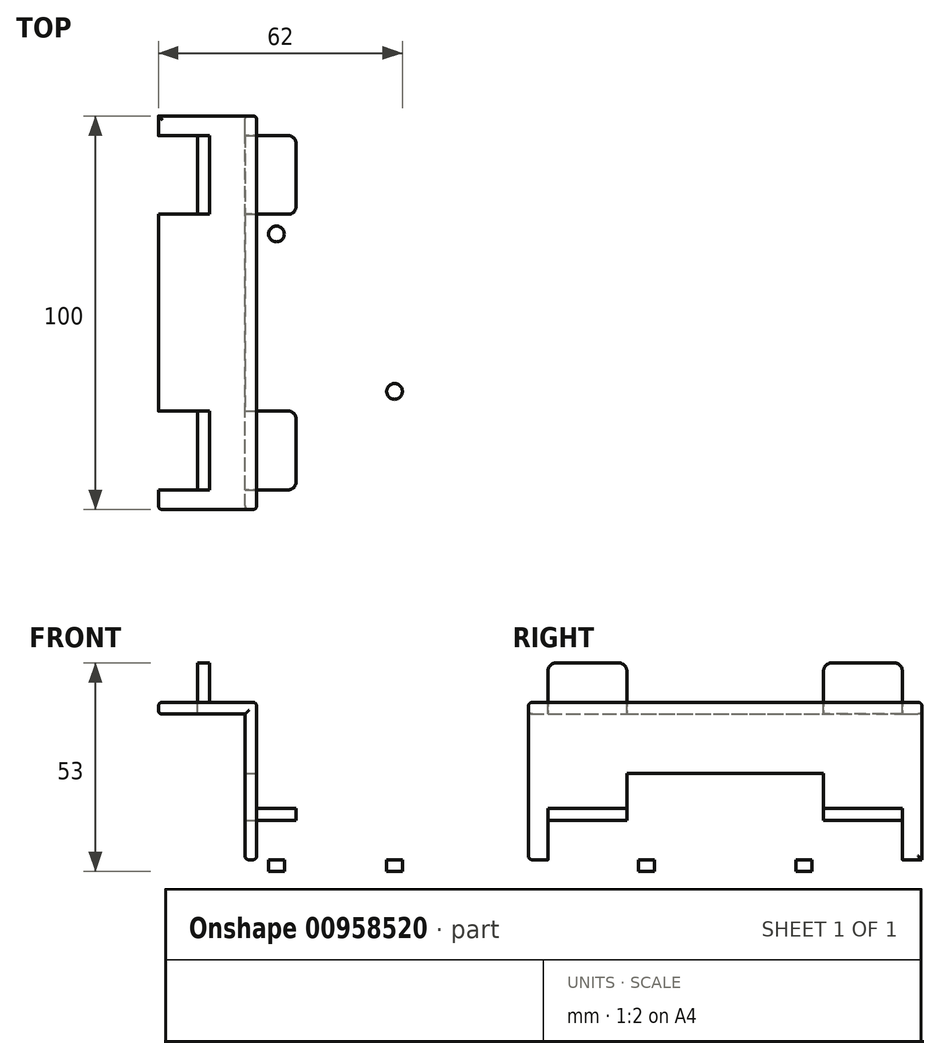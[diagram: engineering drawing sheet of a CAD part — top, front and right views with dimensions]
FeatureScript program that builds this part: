
annotation { "Feature Type Name" : "Feature", "Feature Type Description" : "" }
export const myFeature = defineFeature(function(context is Context, id is Id, definition is map)
    precondition{}
    {
        {
            var Q0;
            Q0=qCreatedBy(makeId("Front.planeOp"),FACE);
            var sketch = newSketch(context, id + "F0", { "sketchPlane" : qUnion([Q0])});
            skLineSegment(sketch, "E0", {"start": v(0, 0) * mm, "end": v(0, 40) * mm});
            skLineSegment(sketch, "E1", {"start": v(0, 40) * mm, "end": v(-25, 40) * mm});
            skLineSegment(sketch, "E2", {"start": v(-25, 40) * mm, "end": v(-25, 37) * mm});
            skLineSegment(sketch, "E3", {"start": v(0, 0) * mm, "end": v(-3, 0) * mm});
            skLineSegment(sketch, "E4", {"start": v(-3, 0) * mm, "end": v(-3, 37) * mm});
            skLineSegment(sketch, "E5", {"start": v(-3, 37) * mm, "end": v(-25, 37) * mm});
            skSolve(sketch);
        }
        {
            var Q0;
            Q0=makeQuery(id+"F0.imprint","IMPRINT",FACE,{"disambiguationData":[TD([[makeQuery(id+"F0.imprint","IMPRINT",EDGE,{"derivedFrom":sQuery(id+"F0.wireOp",EDGE,"E0")}),1.0]])]});
            extrude(context, id + "F1", {"entities" : qUnion([Q0]), "endBound" : BoundingType.SYMMETRIC, "depth" : 100 * mm, "offsetDistance" : 25 * mm});
        }
        {
            var Q0;
            Q0=makeQuery(id+"F1.opExtrude","SWEPT_FACE",FACE,{"disambiguationData":[OSD([sQuery(id+"F0.wireOp",EDGE,"E0")])]});
            var sketch = newSketch(context, id + "F2", { "sketchPlane" : qUnion([Q0])});
            skLineSegment(sketch, "E6.bottom", {"start": v(-45, 0) * mm, "end": v(-25, 0) * mm});
            skLineSegment(sketch, "E6.top", {"start": v(-45, 10) * mm, "end": v(-25, 10) * mm});
            skLineSegment(sketch, "E6.left", {"start": v(-45, 0) * mm, "end": v(-45, 10) * mm});
            skLineSegment(sketch, "E6.right", {"start": v(-25, 0) * mm, "end": v(-25, 10) * mm});
            skLineSegment(sketch, "E7.MirrorCS", {"start": v(25, 0) * mm, "end": v(25, 10) * mm});
            skLineSegment(sketch, "E8.MirrorCS", {"start": v(45, 10) * mm, "end": v(25, 10) * mm});
            skLineSegment(sketch, "E9.MirrorCS", {"start": v(45, 0) * mm, "end": v(45, 10) * mm});
            skLineSegment(sketch, "E10.MirrorCS", {"start": v(45, 0) * mm, "end": v(25, 0) * mm});
            skLineSegment(sketch, "E11.top", {"start": v(-45, 13) * mm, "end": v(-25, 13) * mm});
            skLineSegment(sketch, "E11.left", {"start": v(-45, 10) * mm, "end": v(-45, 13) * mm});
            skLineSegment(sketch, "E11.right", {"start": v(-25, 10) * mm, "end": v(-25, 13) * mm});
            skLineSegment(sketch, "E12.MirrorCS", {"start": v(45, 13) * mm, "end": v(25, 13) * mm});
            skLineSegment(sketch, "E13.MirrorCS", {"start": v(25, 10) * mm, "end": v(25, 13) * mm});
            skLineSegment(sketch, "E14.MirrorCS", {"start": v(45, 10) * mm, "end": v(45, 13) * mm});
            skSolve(sketch);
        }
        {
            var Q0;
            Q0=makeQuery(id+"F2.imprint","IMPRINT",FACE,{"disambiguationData":[TD([[makeQuery(id+"F2.imprint","IMPRINT",EDGE,{"derivedFrom":sQuery(id+"F2.wireOp",EDGE,"E6.bottom")}),1.0]])]});
            var Q1;
            Q1=makeQuery(id+"F2.imprint","IMPRINT",FACE,{"disambiguationData":[TD([[makeQuery(id+"F2.imprint","IMPRINT",EDGE,{"derivedFrom":sQuery(id+"F2.wireOp",EDGE,"E7.MirrorCS")}),-1.0]])]});
            extrude(context, id + "F3", {"entities" : qUnion([Q0, Q1]), "operationType" : NewBodyOperationType.REMOVE, "endBound" : BoundingType.UP_TO_NEXT, "oppositeDirection" : true, "depth" : 25 * mm, "offsetDistance" : 25 * mm});
        }
        {
            var Q0;
            Q0=makeQuery(id+"F2.imprint","IMPRINT",FACE,{"disambiguationData":[TD([[makeQuery(id+"F2.imprint","IMPRINT",EDGE,{"derivedFrom":sQuery(id+"F2.wireOp",EDGE,"E6.top")}),1.0]])]});
            var Q1;
            Q1=makeQuery(id+"F2.imprint","IMPRINT",FACE,{"disambiguationData":[TD([[makeQuery(id+"F2.imprint","IMPRINT",EDGE,{"derivedFrom":sQuery(id+"F2.wireOp",EDGE,"E8.MirrorCS")}),-1.0]])]});
            extrude(context, id + "F4", {"entities" : qUnion([Q0, Q1]), "operationType" : NewBodyOperationType.ADD, "depth" : 10 * mm, "offsetDistance" : 25 * mm});
        }
        {
            var Q0;
            Q0=makeQuery(id+"F1.opExtrude","SWEPT_FACE",FACE,{"disambiguationData":[OSD([sQuery(id+"F0.wireOp",EDGE,"E1")])]});
            var sketch = newSketch(context, id + "F5", { "sketchPlane" : qUnion([Q0])});
            skLineSegment(sketch, "E15.bottom", {"start": v(-25, 45) * mm, "end": v(-15, 45) * mm});
            skLineSegment(sketch, "E15.top", {"start": v(-25, 25) * mm, "end": v(-15, 25) * mm});
            skLineSegment(sketch, "E15.left", {"start": v(-25, 45) * mm, "end": v(-25, 25) * mm});
            skLineSegment(sketch, "E15.right", {"start": v(-15, 45) * mm, "end": v(-15, 25) * mm});
            skLineSegment(sketch, "E16.bottom", {"start": v(-15, 45) * mm, "end": v(-12, 45) * mm});
            skLineSegment(sketch, "E16.top", {"start": v(-15, 25) * mm, "end": v(-12, 25) * mm});
            skLineSegment(sketch, "E16.right", {"start": v(-12, 45) * mm, "end": v(-12, 25) * mm});
            skLineSegment(sketch, "E17.MirrorCS", {"start": v(-25, -25) * mm, "end": v(-15, -25) * mm});
            skLineSegment(sketch, "E18.MirrorCS", {"start": v(-25, -45) * mm, "end": v(-25, -25) * mm});
            skLineSegment(sketch, "E19.MirrorCS", {"start": v(-25, -45) * mm, "end": v(-15, -45) * mm});
            skLineSegment(sketch, "E20.MirrorCS", {"start": v(-15, -45) * mm, "end": v(-15, -25) * mm});
            skLineSegment(sketch, "E21.MirrorCS", {"start": v(-15, -45) * mm, "end": v(-12, -45) * mm});
            skLineSegment(sketch, "E22.MirrorCS", {"start": v(-12, -45) * mm, "end": v(-12, -25) * mm});
            skLineSegment(sketch, "E23.MirrorCS", {"start": v(-15, -25) * mm, "end": v(-12, -25) * mm});
            skSolve(sketch);
        }
        {
            var Q0;
            Q0=makeQuery(id+"F5.imprint","IMPRINT",FACE,{"disambiguationData":[TD([[makeQuery(id+"F5.imprint","IMPRINT",EDGE,{"derivedFrom":sQuery(id+"F5.wireOp",EDGE,"E15.bottom")}),-1.0]])]});
            var Q1;
            Q1=makeQuery(id+"F5.imprint","IMPRINT",FACE,{"disambiguationData":[TD([[makeQuery(id+"F5.imprint","IMPRINT",EDGE,{"derivedFrom":sQuery(id+"F5.wireOp",EDGE,"E17.MirrorCS")}),-1.0]])]});
            extrude(context, id + "F6", {"entities" : qUnion([Q0, Q1]), "operationType" : NewBodyOperationType.REMOVE, "endBound" : BoundingType.UP_TO_NEXT, "oppositeDirection" : true, "depth" : 25 * mm, "offsetDistance" : 25 * mm});
        }
        {
            var Q0;
            Q0=makeQuery(id+"F5.imprint","IMPRINT",FACE,{"disambiguationData":[TD([[makeQuery(id+"F5.imprint","IMPRINT",EDGE,{"derivedFrom":sQuery(id+"F5.wireOp",EDGE,"E16.bottom")}),-1.0]])]});
            var Q1;
            Q1=makeQuery(id+"F5.imprint","IMPRINT",FACE,{"disambiguationData":[TD([[makeQuery(id+"F5.imprint","IMPRINT",EDGE,{"derivedFrom":sQuery(id+"F5.wireOp",EDGE,"E20.MirrorCS")}),-1.0]])]});
            extrude(context, id + "F7", {"entities" : qUnion([Q0, Q1]), "operationType" : NewBodyOperationType.ADD, "depth" : 10 * mm, "offsetDistance" : 25 * mm});
        }
        {
            var Q0;
            Q0=makeQuery(id+"F7.opExtrude","CAP_EDGE",EDGE,{"disambiguationData":[OSD([sQuery(id+"F5.wireOp",EDGE,"E16.top")])],"isStart":false});
            var Q1;
            Q1=makeQuery(id+"F7.opExtrude","CAP_EDGE",EDGE,{"disambiguationData":[OSD([sQuery(id+"F5.wireOp",EDGE,"E16.bottom")])],"isStart":false});
            var Q2;
            Q2=makeQuery(id+"F7.opExtrude","CAP_EDGE",EDGE,{"disambiguationData":[OSD([sQuery(id+"F5.wireOp",EDGE,"E23.MirrorCS")])],"isStart":false});
            var Q3;
            Q3=makeQuery(id+"F7.opExtrude","CAP_EDGE",EDGE,{"disambiguationData":[OSD([sQuery(id+"F5.wireOp",EDGE,"E21.MirrorCS")])],"isStart":false});
            var Q4;
            Q4=makeQuery(id+"F4.opExtrude","CAP_EDGE",EDGE,{"disambiguationData":[OSD([sQuery(id+"F2.wireOp",EDGE,"E11.left")])],"isStart":false});
            var Q5;
            Q5=makeQuery(id+"F4.opExtrude","CAP_EDGE",EDGE,{"disambiguationData":[OSD([sQuery(id+"F2.wireOp",EDGE,"E11.right")])],"isStart":false});
            var Q6;
            Q6=makeQuery(id+"F4.opExtrude","CAP_EDGE",EDGE,{"disambiguationData":[OSD([sQuery(id+"F2.wireOp",EDGE,"E13.MirrorCS")])],"isStart":false});
            var Q7;
            Q7=makeQuery(id+"F4.opExtrude","CAP_EDGE",EDGE,{"disambiguationData":[OSD([sQuery(id+"F2.wireOp",EDGE,"E14.MirrorCS")])],"isStart":false});
            fillet(context, id + "F8", {"entities" : qUnion([Q0, Q1, Q2, Q3, Q4, Q5, Q6, Q7]), "radius" : 2 * mm, "tangentPropagation" : true, "allowEdgeOverflow" : false});
        }
        {
            var Q0;
            Q0=makeQuery(id+"F1.opExtrude","CAP_EDGE",EDGE,{"disambiguationData":[OSD([sQuery(id+"F0.wireOp",EDGE,"E1")])],"isStart":false});
            var Q1;
            Q1=makeQuery(id+"F1.opExtrude","CAP_EDGE",EDGE,{"disambiguationData":[OSD([sQuery(id+"F0.wireOp",EDGE,"E0")])],"isStart":false});
            var Q2;
            Q2=makeQuery(id+"F1.opExtrude","CAP_EDGE",EDGE,{"disambiguationData":[OSD([sQuery(id+"F0.wireOp",EDGE,"E4")])],"isStart":false});
            var Q3;
            Q3=makeQuery(id+"F1.opExtrude","CAP_EDGE",EDGE,{"disambiguationData":[OSD([sQuery(id+"F0.wireOp",EDGE,"E5")])],"isStart":false});
            fillet(context, id + "F9", {"entities" : qUnion([Q0, Q1, Q2, Q3]), "radius" : 1 * mm, "tangentPropagation" : true, "allowEdgeOverflow" : false});
        }
        {
            var Q0;
            {var subQ0=sQuery(id+"F0.wireOp",EDGE,"E5");var subQ1=sQuery(id+"F0.wireOp",EDGE,"E2");Q0=makeQuery(id+"F6.boolean.opBoolean","SPLIT",EDGE,{"disambiguationData":[TD([makeQuery(id+"F6.opExtrude","SWEPT_FACE",FACE,{"disambiguationData":[OSD([sQuery(id+"F5.wireOp",EDGE,"E19.MirrorCS")])]})])],"derivedFrom":makeQuery(id+"F1.opExtrude","SWEPT_EDGE",EDGE,{"disambiguationData":[OSD([subQ1,subQ0])]})});}
            var Q1;
            {var subQ0=sQuery(id+"F0.wireOp",EDGE,"E2");var subQ1=sQuery(id+"F0.wireOp",EDGE,"E1");Q1=makeQuery(id+"F6.boolean.opBoolean","SPLIT",EDGE,{"disambiguationData":[TD([makeQuery(id+"F6.opExtrude","SWEPT_FACE",FACE,{"disambiguationData":[OSD([sQuery(id+"F5.wireOp",EDGE,"E19.MirrorCS")])]})])],"derivedFrom":makeQuery(id+"F1.opExtrude","SWEPT_EDGE",EDGE,{"disambiguationData":[OSD([subQ1,subQ0])]})});}
            fillet(context, id + "F10", {"entities" : qUnion([Q0, Q1]), "radius" : 1 * mm, "tangentPropagation" : true, "allowEdgeOverflow" : false});
        }
        {
            var Q0;
            {var subQ0=sQuery(id+"F0.wireOp",EDGE,"E1");var subQ1=sQuery(id+"F0.wireOp",EDGE,"E2");Q0=makeQuery(id+"F6.boolean.opBoolean","SPLIT",EDGE,{"disambiguationData":[TD([makeQuery(id+"F6.opExtrude","SWEPT_FACE",FACE,{"disambiguationData":[OSD([sQuery(id+"F5.wireOp",EDGE,"E15.top")])]})])],"derivedFrom":makeQuery(id+"F1.opExtrude","SWEPT_EDGE",EDGE,{"disambiguationData":[OSD([subQ0,subQ1])]})});}
            var Q1;
            {var subQ0=sQuery(id+"F0.wireOp",EDGE,"E2");var subQ1=sQuery(id+"F0.wireOp",EDGE,"E5");Q1=makeQuery(id+"F6.boolean.opBoolean","SPLIT",EDGE,{"disambiguationData":[TD([makeQuery(id+"F6.opExtrude","SWEPT_FACE",FACE,{"disambiguationData":[OSD([sQuery(id+"F5.wireOp",EDGE,"E15.top")])]})])],"derivedFrom":makeQuery(id+"F1.opExtrude","SWEPT_EDGE",EDGE,{"disambiguationData":[OSD([subQ0,subQ1])]})});}
            var Q2;
            {var subQ0=sQuery(id+"F0.wireOp",EDGE,"E2");var subQ1=sQuery(id+"F0.wireOp",EDGE,"E1");Q2=makeQuery(id+"F6.boolean.opBoolean","SPLIT",EDGE,{"disambiguationData":[TD([makeQuery(id+"F6.opExtrude","SWEPT_FACE",FACE,{"disambiguationData":[OSD([sQuery(id+"F5.wireOp",EDGE,"E15.bottom")])]})])],"derivedFrom":makeQuery(id+"F1.opExtrude","SWEPT_EDGE",EDGE,{"disambiguationData":[OSD([subQ1,subQ0])]})});}
            var Q3;
            {var subQ0=sQuery(id+"F0.wireOp",EDGE,"E5");var subQ1=sQuery(id+"F0.wireOp",EDGE,"E2");Q3=makeQuery(id+"F6.boolean.opBoolean","SPLIT",EDGE,{"disambiguationData":[TD([makeQuery(id+"F6.opExtrude","SWEPT_FACE",FACE,{"disambiguationData":[OSD([sQuery(id+"F5.wireOp",EDGE,"E15.bottom")])]})])],"derivedFrom":makeQuery(id+"F1.opExtrude","SWEPT_EDGE",EDGE,{"disambiguationData":[OSD([subQ1,subQ0])]})});}
            var Q4;
            Q4=makeQuery(id+"F1.opExtrude","CAP_EDGE",EDGE,{"disambiguationData":[OSD([sQuery(id+"F0.wireOp",EDGE,"E5")])],"isStart":true});
            var Q5;
            Q5=makeQuery(id+"F1.opExtrude","CAP_EDGE",EDGE,{"disambiguationData":[OSD([sQuery(id+"F0.wireOp",EDGE,"E1")])],"isStart":true});
            var Q6;
            Q6=makeQuery(id+"F1.opExtrude","CAP_EDGE",EDGE,{"disambiguationData":[OSD([sQuery(id+"F0.wireOp",EDGE,"E4")])],"isStart":true});
            var Q7;
            Q7=makeQuery(id+"F1.opExtrude","CAP_EDGE",EDGE,{"disambiguationData":[OSD([sQuery(id+"F0.wireOp",EDGE,"E0")])],"isStart":true});
            var Q8;
            {var subQ0=sQuery(id+"F0.wireOp",EDGE,"E4");var subQ1=sQuery(id+"F0.wireOp",EDGE,"E3");Q8=makeQuery(id+"F3.boolean.opBoolean","SPLIT",EDGE,{"disambiguationData":[TD([makeQuery(id+"F3.opExtrude","SWEPT_FACE",FACE,{"disambiguationData":[OSD([sQuery(id+"F2.wireOp",EDGE,"E9.MirrorCS")])]})])],"derivedFrom":makeQuery(id+"F1.opExtrude","SWEPT_EDGE",EDGE,{"disambiguationData":[OSD([subQ1,subQ0])]})});}
            var Q9;
            {var subQ0=sQuery(id+"F0.wireOp",EDGE,"E0");var subQ1=sQuery(id+"F0.wireOp",EDGE,"E3");Q9=makeQuery(id+"F3.boolean.opBoolean","SPLIT",EDGE,{"disambiguationData":[TD([makeQuery(id+"F3.opExtrude","SWEPT_FACE",FACE,{"disambiguationData":[OSD([sQuery(id+"F2.wireOp",EDGE,"E9.MirrorCS")])]})])],"derivedFrom":makeQuery(id+"F1.opExtrude","SWEPT_EDGE",EDGE,{"disambiguationData":[OSD([subQ0,subQ1])]})});}
            var Q10;
            {var subQ0=sQuery(id+"F0.wireOp",EDGE,"E4");var subQ1=sQuery(id+"F0.wireOp",EDGE,"E3");Q10=makeQuery(id+"F3.boolean.opBoolean","SPLIT",EDGE,{"disambiguationData":[TD([makeQuery(id+"F3.opExtrude","SWEPT_FACE",FACE,{"disambiguationData":[OSD([sQuery(id+"F2.wireOp",EDGE,"E6.left")])]})])],"derivedFrom":makeQuery(id+"F1.opExtrude","SWEPT_EDGE",EDGE,{"disambiguationData":[OSD([subQ1,subQ0])]})});}
            var Q11;
            {var subQ0=sQuery(id+"F0.wireOp",EDGE,"E0");var subQ1=sQuery(id+"F0.wireOp",EDGE,"E3");Q11=makeQuery(id+"F3.boolean.opBoolean","SPLIT",EDGE,{"disambiguationData":[TD([makeQuery(id+"F3.opExtrude","SWEPT_FACE",FACE,{"disambiguationData":[OSD([sQuery(id+"F2.wireOp",EDGE,"E6.left")])]})])],"derivedFrom":makeQuery(id+"F1.opExtrude","SWEPT_EDGE",EDGE,{"disambiguationData":[OSD([subQ0,subQ1])]})});}
            fillet(context, id + "F11", {"entities" : qUnion([Q0, Q1, Q2, Q3, Q4, Q5, Q6, Q7, Q8, Q9, Q10, Q11]), "radius" : 1 * mm, "tangentPropagation" : true, "allowEdgeOverflow" : false});
        }
        {
            var Q0;
            Q0=makeQuery(id+"F1.opExtrude","SWEPT_EDGE",EDGE,{"disambiguationData":[OSD([sQuery(id+"F0.wireOp",EDGE,"E0"),sQuery(id+"F0.wireOp",EDGE,"E1")])]});
            fillet(context, id + "F12", {"entities" : qUnion([Q0]), "radius" : 1 * mm, "tangentPropagation" : true, "allowEdgeOverflow" : false});
        }
        {
            var Q0;
            Q0=qCreatedBy(makeId("Right.planeOp"),FACE);
            var sketch = newSketch(context, id + "F13", { "sketchPlane" : qUnion([Q0])});
            skLineSegment(sketch, "E24.bottom", {"start": v(-25, 0) * mm, "end": v(25, 0) * mm});
            skLineSegment(sketch, "E24.top", {"start": v(-25, -3) * mm, "end": v(25, -3) * mm});
            skLineSegment(sketch, "E24.left", {"start": v(-25, 0) * mm, "end": v(-25, -3) * mm});
            skLineSegment(sketch, "E24.right", {"start": v(25, 0) * mm, "end": v(25, -3) * mm});
            skSolve(sketch);
        }
        {
            var Q0;
            Q0=makeQuery(id+"F13.imprint","IMPRINT",FACE,{"disambiguationData":[TD([[makeQuery(id+"F13.imprint","IMPRINT",EDGE,{"derivedFrom":sQuery(id+"F13.wireOp",EDGE,"E24.bottom")}),-1.0]])]});
            extrude(context, id + "F14", {"entities" : qUnion([Q0]), "operationType" : NewBodyOperationType.ADD, "oppositeDirection" : true, "depth" : 23 * mm, "offsetDistance" : 25 * mm});
        }
        {
            var Q0;
            Q0=makeQuery(id+"F14.boolean.opBoolean","MERGE",FACE,{"derivedFrom":[makeQuery(id+"F1.opExtrude","SWEPT_FACE",FACE,{"disambiguationData":[OSD([sQuery(id+"F0.wireOp",EDGE,"E0")])]}),makeQuery(id+"F14.opExtrude","CAP_FACE",FACE,{"disambiguationData":[OSD([sQuery(id+"F13.wireOp",EDGE,"E24.bottom"),sQuery(id+"F13.wireOp",EDGE,"E24.top"),sQuery(id+"F13.wireOp",EDGE,"E24.left"),sQuery(id+"F13.wireOp",EDGE,"E24.right")])],"isStart":true})]});
            var sketch = newSketch(context, id + "F15", { "sketchPlane" : qUnion([Q0])});
            skLineSegment(sketch, "E25.bottom", {"start": v(-25, -3) * mm, "end": v(25, -3) * mm});
            skLineSegment(sketch, "E25.top", {"start": v(-25, 0) * mm, "end": v(25, 0) * mm});
            skLineSegment(sketch, "E25.left", {"start": v(-25, -3) * mm, "end": v(-25, 0) * mm});
            skLineSegment(sketch, "E25.right", {"start": v(25, -3) * mm, "end": v(25, 0) * mm});
            skSolve(sketch);
        }
        {
            var Q0;
            Q0=makeQuery(id+"F15.imprint","IMPRINT",FACE,{"disambiguationData":[TD([[makeQuery(id+"F15.imprint","IMPRINT",EDGE,{"derivedFrom":sQuery(id+"F15.wireOp",EDGE,"E25.bottom")}),1.0]])]});
            extrude(context, id + "F16", {"entities" : qUnion([Q0]), "operationType" : NewBodyOperationType.ADD, "depth" : 40 * mm, "offsetDistance" : 25 * mm});
        }
        {
            var Q0;
            Q0=makeQuery(id+"F16.boolean.opBoolean","MERGE",FACE,{"derivedFrom":[makeQuery(id+"F14.opExtrude","SWEPT_FACE",FACE,{"disambiguationData":[OSD([sQuery(id+"F13.wireOp",EDGE,"E24.top")])]}),makeQuery(id+"F16.opExtrude","SWEPT_FACE",FACE,{"disambiguationData":[OSD([sQuery(id+"F15.wireOp",EDGE,"E25.bottom")])]})]});
            var sketch = newSketch(context, id + "F17", { "sketchPlane" : qUnion([Q0])});
            skLineSegment(sketch, "E26", {"start": v(0, 0) * mm, "end": v(40, 0) * mm, "construction": true});
            skLineSegment(sketch, "E27", {"start": v(20, 25) * mm, "end": v(20, 0) * mm, "construction": true});
            skPoint(sketch, "E27.startSnap0", {"position": v(20, 0) * mm});
            skCircle(sketch, "E28", {"center": v(20, 0) * mm, "radius": 10 * mm});
            skLineSegment(sketch, "E29", {"start": v(0, 0) * mm, "end": v(0, 25) * mm, "construction": true});
            skLineSegment(sketch, "E30", {"start": v(0, 25) * mm, "end": v(20, 25) * mm, "construction": true});
            skCircle(sketch, "E31", {"center": v(5, 20) * mm, "radius": 2 * mm});
            skCircle(sketch, "E32.MirrorC", {"center": v(5, -20) * mm, "radius": 2 * mm});
            skCircle(sketch, "E33.MirrorC", {"center": v(35, 20) * mm, "radius": 2 * mm});
            skCircle(sketch, "E34.MirrorC", {"center": v(35, -20) * mm, "radius": 2 * mm});
            skSolve(sketch);
        }
        {
            var Q0;
            Q0=makeQuery(id+"F17.imprint","IMPRINT",FACE,{"disambiguationData":[TD([[makeQuery(id+"F17.imprint","IMPRINT",EDGE,{"derivedFrom":sQuery(id+"F17.wireOp",EDGE,"E33.MirrorC")}),-1.0]])]});
            var Q1;
            Q1=makeQuery(id+"F17.imprint","IMPRINT",FACE,{"disambiguationData":[TD([[makeQuery(id+"F17.imprint","IMPRINT",EDGE,{"derivedFrom":sQuery(id+"F17.wireOp",EDGE,"E31")}),1.0]])]});
            var Q2;
            Q2=makeQuery(id+"F17.imprint","IMPRINT",FACE,{"disambiguationData":[TD([[makeQuery(id+"F17.imprint","IMPRINT",EDGE,{"derivedFrom":sQuery(id+"F17.wireOp",EDGE,"E28")}),1.0]])]});
            var Q3;
            Q3=makeQuery(id+"F17.imprint","IMPRINT",FACE,{"disambiguationData":[TD([[makeQuery(id+"F17.imprint","IMPRINT",EDGE,{"derivedFrom":sQuery(id+"F17.wireOp",EDGE,"E34.MirrorC")}),1.0]])]});
            var Q4;
            Q4=makeQuery(id+"F17.imprint","IMPRINT",FACE,{"disambiguationData":[TD([[makeQuery(id+"F17.imprint","IMPRINT",EDGE,{"derivedFrom":sQuery(id+"F17.wireOp",EDGE,"E32.MirrorC")}),-1.0]])]});
            extrude(context, id + "F18", {"entities" : qUnion([Q0, Q1, Q2, Q3, Q4]), "operationType" : NewBodyOperationType.REMOVE, "oppositeDirection" : true, "depth" : 25 * mm, "offsetDistance" : 25 * mm});
        }
    });
